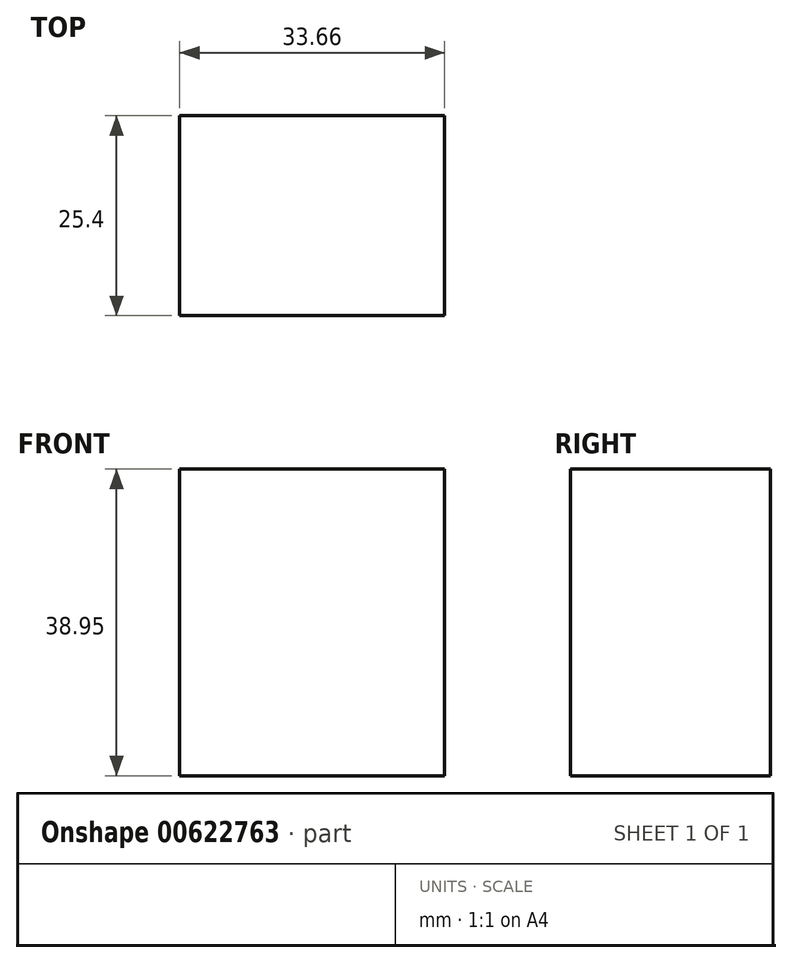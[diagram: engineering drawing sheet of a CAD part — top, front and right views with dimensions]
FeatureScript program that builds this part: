
annotation { "Feature Type Name" : "Feature", "Feature Type Description" : "" }
export const myFeature = defineFeature(function(context is Context, id is Id, definition is map)
    precondition{}
    {
        {
            var Q0;
            Q0=qCreatedBy(makeId("Front.planeOp"),FACE);
            var sketch = newSketch(context, id + "F0", { "sketchPlane" : qUnion([Q0])});
            skLineSegment(sketch, "E0.bottom", {"start": v(-65.2, 56.59) * mm, "end": v(-31.54, 56.59) * mm});
            skLineSegment(sketch, "E0.top", {"start": v(-65.2, 17.64) * mm, "end": v(-31.54, 17.64) * mm});
            skLineSegment(sketch, "E0.left", {"start": v(-65.2, 56.59) * mm, "end": v(-65.2, 17.64) * mm});
            skLineSegment(sketch, "E0.right", {"start": v(-31.54, 56.59) * mm, "end": v(-31.54, 17.64) * mm});
            skSolve(sketch);
        }
        {
            var Q0;
            Q0 = qSketchRegion(id + "F0", true);
            extrude(context, id + "F1", {"entities" : qUnion([Q0]), "depth" : 25.4 * mm, "offsetDistance" : 25.4 * mm});
        }
    });
